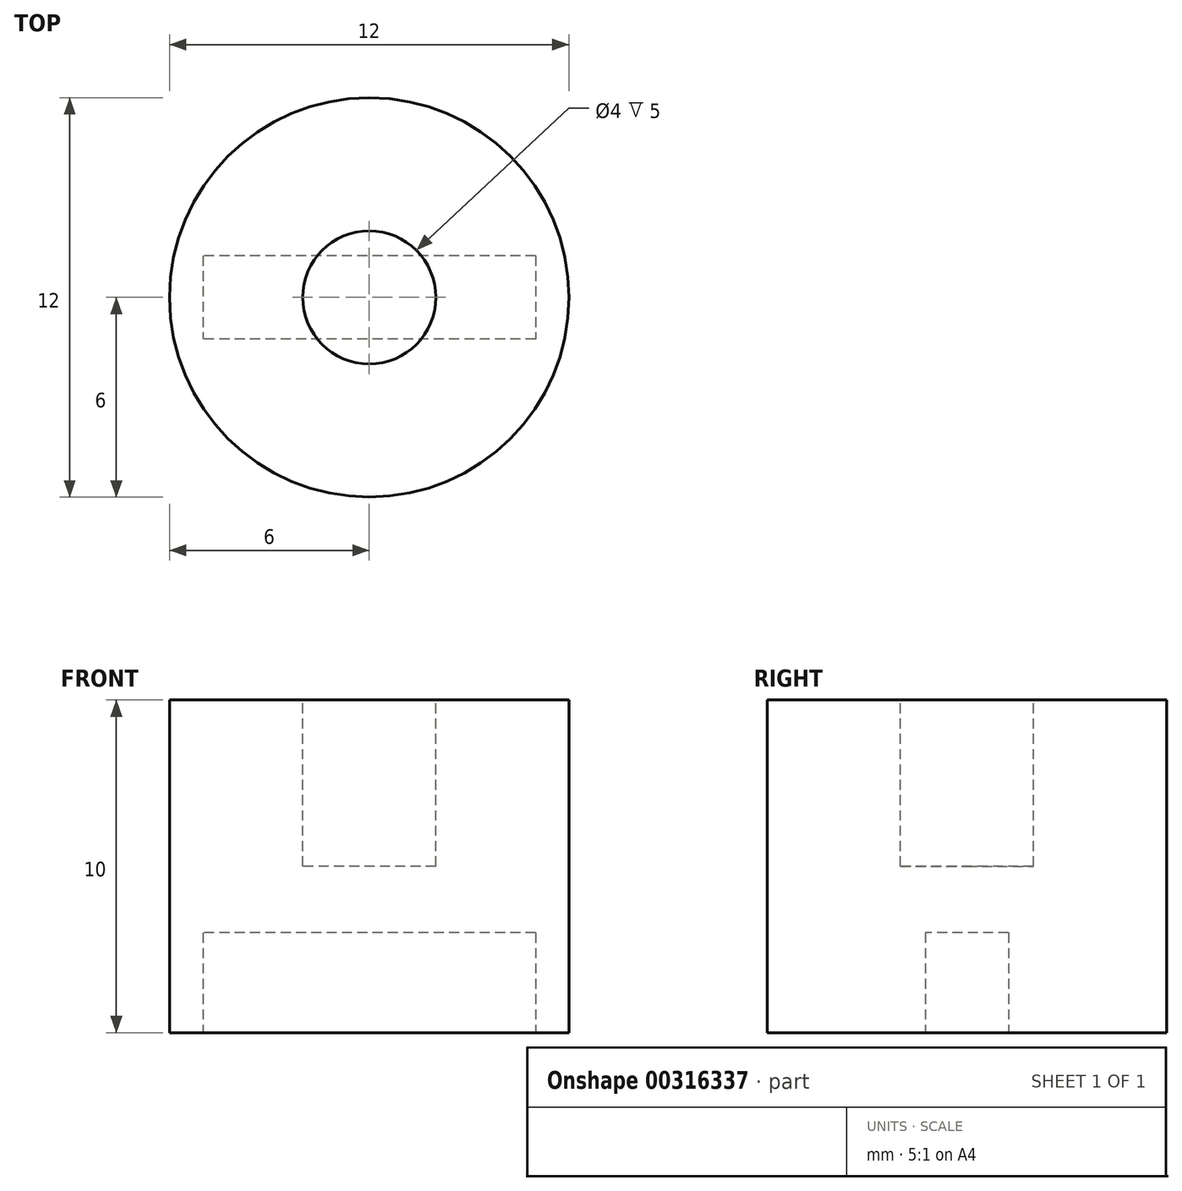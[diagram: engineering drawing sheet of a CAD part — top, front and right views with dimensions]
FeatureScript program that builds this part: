
annotation { "Feature Type Name" : "Feature", "Feature Type Description" : "" }
export const myFeature = defineFeature(function(context is Context, id is Id, definition is map)
    precondition{}
    {
        {
            var Q0;
            Q0=qCreatedBy(makeId("Top.planeOp"),FACE);
            var sketch = newSketch(context, id + "F0", { "sketchPlane" : qUnion([Q0])});
            skCircle(sketch, "E0", {"center": v(0, 0) * mm, "radius": 6 * mm});
            skLineSegment(sketch, "E1", {"start": v(0, 11.26) * mm, "end": v(0, -8.77) * mm});
            skLineSegment(sketch, "E2", {"start": v(0, -8.77) * mm, "end": v(0, 11.26) * mm, "construction": true});
            skSolve(sketch);
        }
        {
            var Q0;
            Q0 = qSketchRegion(id + "F0", true);
            extrude(context, id + "F1", {"entities" : qUnion([Q0]), "depth" : 10 * mm});
        }
        {
            var Q0;
            Q0=makeQuery(id+"F1.opExtrude","CAP_FACE",FACE,{"disambiguationData":[OSD([sQuery(id+"F0.wireOp",EDGE,"E0"),sQuery(id+"F0.wireOp",EDGE,"DOAHkpi3-Hd2K-uk01-UViC-ww1lmG4igD3E"),sQuery(id+"F0.wireOp",EDGE,"f3206277-f84b-4ad1-9b42-8c7db3e1b2c00.MirrorC")])],"isStart":false});
            var sketch = newSketch(context, id + "F2", { "sketchPlane" : qUnion([Q0])});
            skCircle(sketch, "E3", {"center": v(0, 0) * mm, "radius": 2 * mm});
            skSolve(sketch);
        }
        {
            var Q0;
            Q0=makeQuery(id+"F2.imprint","IMPRINT",FACE,{"disambiguationData":[TD([[makeQuery(id+"F2.imprint","IMPRINT",EDGE,{"derivedFrom":sQuery(id+"F2.wireOp",EDGE,"E3")}),1.0]])]});
            extrude(context, id + "F3", {"entities" : qUnion([Q0]), "operationType" : NewBodyOperationType.REMOVE, "oppositeDirection" : true, "depth" : 5 * mm});
        }
        {
            var Q0;
            Q0=makeQuery(id+"F1.opExtrude","CAP_FACE",FACE,{"disambiguationData":[OSD([sQuery(id+"F0.wireOp",EDGE,"E0")])],"isStart":true});
            var sketch = newSketch(context, id + "F4", { "sketchPlane" : qUnion([Q0])});
            skLineSegment(sketch, "E4.bottom", {"start": v(5, -1.25) * mm, "end": v(-5, -1.25) * mm});
            skLineSegment(sketch, "E4.top", {"start": v(5, 1.25) * mm, "end": v(-5, 1.25) * mm});
            skLineSegment(sketch, "E4.left", {"start": v(5, -1.25) * mm, "end": v(5, 1.25) * mm});
            skLineSegment(sketch, "E4.right", {"start": v(-5, -1.25) * mm, "end": v(-5, 1.25) * mm});
            skPoint(sketch, "E4.middle", {"position": v(0, 0) * mm});
            skSolve(sketch);
        }
        {
            var Q0;
            Q0=makeQuery(id+"F4.imprint","IMPRINT",FACE,{"disambiguationData":[TD([[makeQuery(id+"F4.imprint","IMPRINT",EDGE,{"derivedFrom":sQuery(id+"F4.wireOp",EDGE,"E4.bottom")}),-1.0]])]});
            extrude(context, id + "F5", {"entities" : qUnion([Q0]), "operationType" : NewBodyOperationType.REMOVE, "oppositeDirection" : true, "depth" : 3 * mm});
        }
    });
